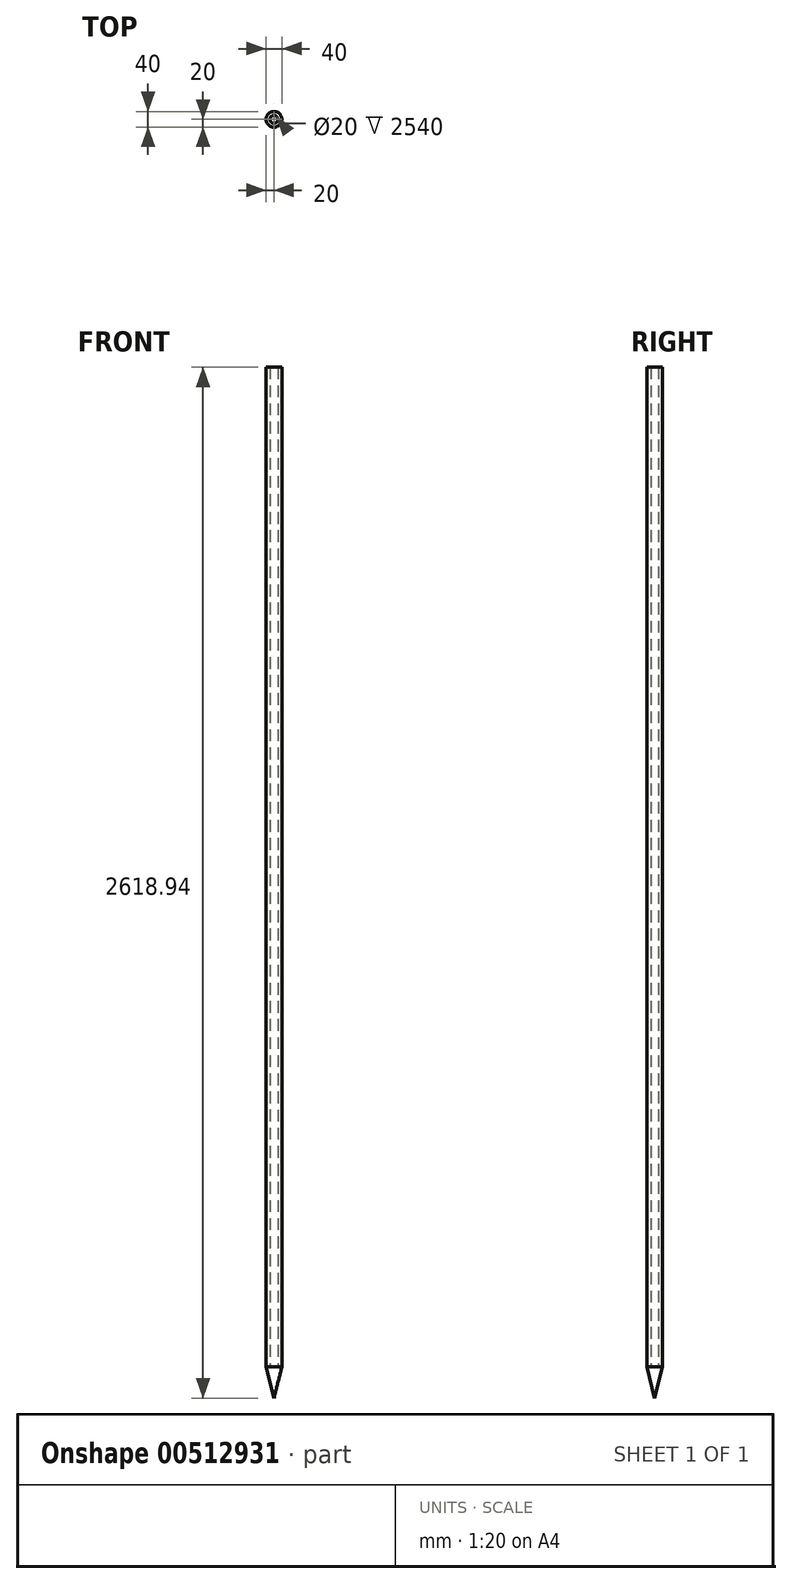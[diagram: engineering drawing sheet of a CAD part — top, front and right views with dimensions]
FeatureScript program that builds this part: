
annotation { "Feature Type Name" : "Feature", "Feature Type Description" : "" }
export const myFeature = defineFeature(function(context is Context, id is Id, definition is map)
    precondition{}
    {
        {
            var Q0;
            Q0=qCreatedBy(makeId("Top.planeOp"),FACE);
            var sketch = newSketch(context, id + "F0", { "sketchPlane" : qUnion([Q0])});
            skPoint(sketch, "E0.center.orphan", {"position": v(12.39, 0) * mm});
            skCircle(sketch, "E1", {"center": v(0, 0) * mm, "radius": 20 * mm});
            skCircle(sketch, "E2", {"center": v(0, 0) * mm, "radius": 10 * mm});
            skSolve(sketch);
        }
        {
            var Q0;
            Q0=makeQuery(id+"F0.imprint","IMPRINT",FACE,{"disambiguationData":[TD([[makeQuery(id+"F0.imprint","IMPRINT",EDGE,{"derivedFrom":sQuery(id+"F0.wireOp",EDGE,"E1")}),1.0]])]});
            var Q1;
            Q1=sQuery(id+"F0.wireOp",EDGE,"E2");
            var Q2;
            Q2=sQuery(id+"F0.wireOp",EDGE,"E1");
            extrude(context, id + "F1", {"entities" : qUnion([Q0]), "surfaceEntities" : qUnion([Q1, Q2]), "depth" : 2540 * mm});
        }
        {
            var Q0;
            Q0=qCreatedBy(makeId("Top.planeOp"),FACE);
            var sketch = newSketch(context, id + "F2", { "sketchPlane" : qUnion([Q0])});
            skCircle(sketch, "E3.0", {"center": v(0, 0) * mm, "radius": 20 * mm});
            skSolve(sketch);
        }
        {
            var Q0;
            Q0=qCreatedBy(makeId("Right.planeOp"),FACE);
            var sketch = newSketch(context, id + "F3", { "sketchPlane" : qUnion([Q0])});
            skLineSegment(sketch, "E4", {"start": v(0, 0) * mm, "end": v(0, -78.94) * mm});
            skLineSegment(sketch, "E5", {"start": v(0, 0) * mm, "end": v(20, 0) * mm});
            skLineSegment(sketch, "E6", {"start": v(20, 0) * mm, "end": v(0, -78.94) * mm});
            skSolve(sketch);
        }
        {
            var Q0;
            Q0=makeQuery(id+"F3.imprint","IMPRINT",FACE,{"disambiguationData":[TD([[makeQuery(id+"F3.imprint","IMPRINT",EDGE,{"derivedFrom":sQuery(id+"F3.wireOp",EDGE,"E4")}),1.0]])]});
            var Q1;
            Q1=sQuery(id+"F3.wireOp",EDGE,"E4");
            revolve(context, id + "F4", {"operationType" : NewBodyOperationType.ADD, "entities" : qUnion([Q0]), "axis" : qUnion([Q1]), "revolveType" : RevolveType.FULL});
        }
    });
